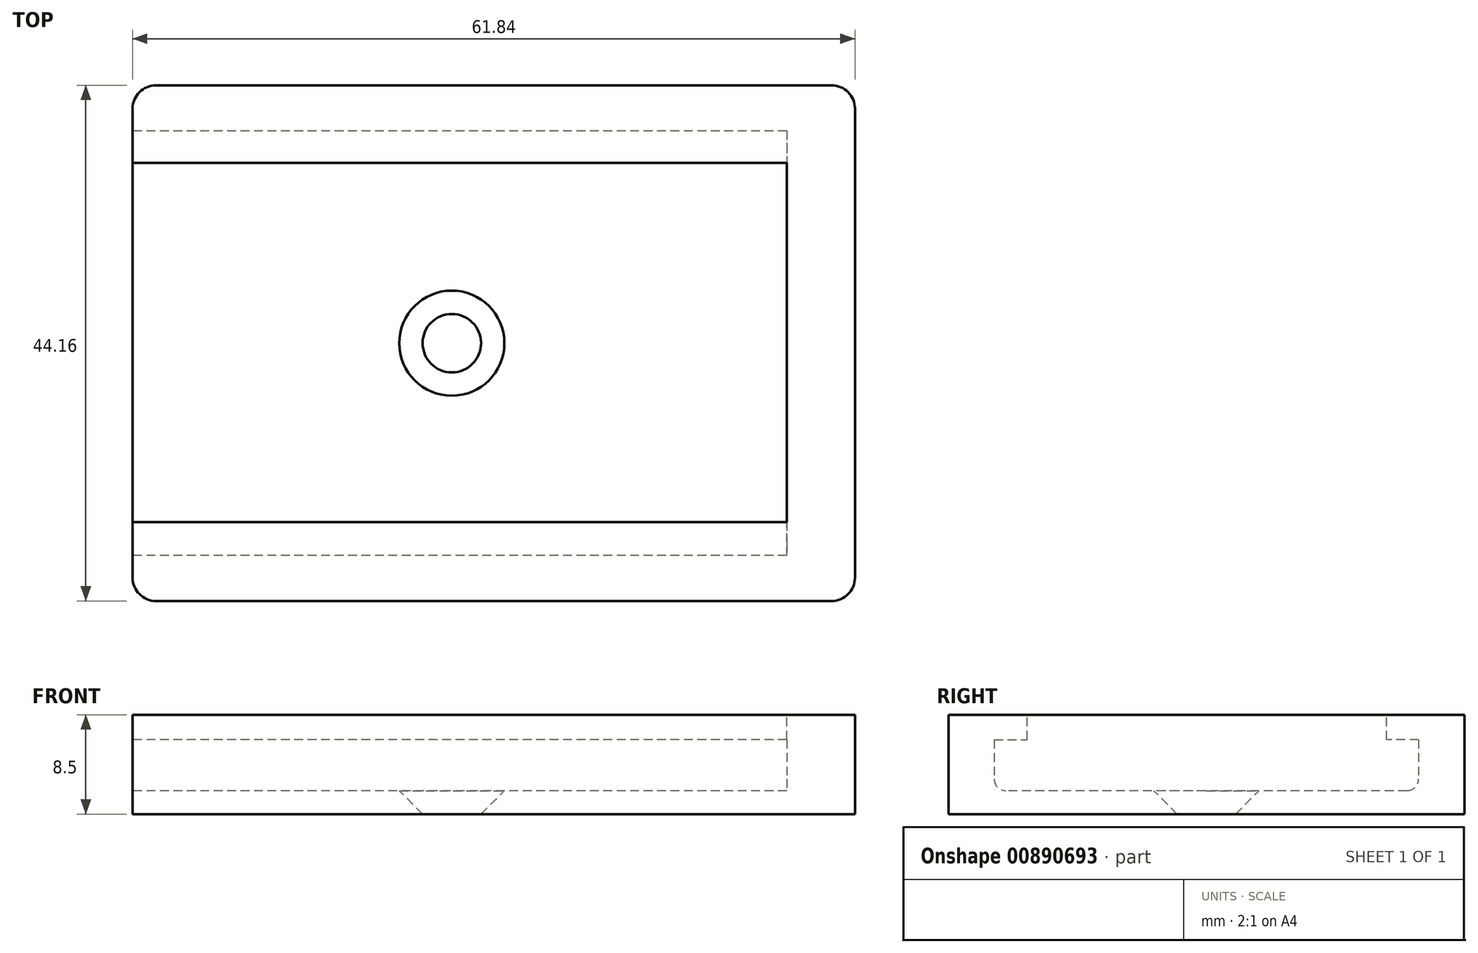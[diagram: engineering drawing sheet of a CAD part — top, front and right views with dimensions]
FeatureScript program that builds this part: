
annotation { "Feature Type Name" : "Feature", "Feature Type Description" : "" }
export const myFeature = defineFeature(function(context is Context, id is Id, definition is map)
    precondition{}
    {
        {
            var Q0;
            Q0=qCreatedBy(makeId("Top.planeOp"),FACE);
            var sketch = newSketch(context, id + "F0", { "sketchPlane" : qUnion([Q0])});
            skLineSegment(sketch, "E0.bottom", {"start": v(-27.33, 22.08) * mm, "end": v(34.5, 22.08) * mm});
            skLineSegment(sketch, "E0.top", {"start": v(-27.33, -22.08) * mm, "end": v(34.5, -22.08) * mm});
            skLineSegment(sketch, "E0.left", {"start": v(-27.33, 22.08) * mm, "end": v(-27.33, -22.08) * mm});
            skLineSegment(sketch, "E0.right", {"start": v(34.5, 22.08) * mm, "end": v(34.5, -22.08) * mm});
            skSolve(sketch);
        }
        {
            var Q0;
            Q0=makeQuery(id+"F0.imprint","IMPRINT",FACE,{"disambiguationData":[TD([[makeQuery(id+"F0.imprint","IMPRINT",EDGE,{"derivedFrom":sQuery(id+"F0.wireOp",EDGE,"E0.bottom")}),-1.0]])]});
            extrude(context, id + "F1", {"entities" : qUnion([Q0]), "depth" : 8.5 * mm, "offsetDistance" : 25 * mm});
        }
        {
            var Q0;
            Q0=makeQuery(id+"F1.opExtrude","SWEPT_EDGE",EDGE,{"disambiguationData":[OSD([sQuery(id+"F0.wireOp",EDGE,"E0.top"),sQuery(id+"F0.wireOp",EDGE,"E0.left")])]});
            var Q1;
            Q1=makeQuery(id+"F1.opExtrude","SWEPT_EDGE",EDGE,{"disambiguationData":[OSD([sQuery(id+"F0.wireOp",EDGE,"E0.top"),sQuery(id+"F0.wireOp",EDGE,"E0.right")])]});
            var Q2;
            Q2=makeQuery(id+"F1.opExtrude","SWEPT_EDGE",EDGE,{"disambiguationData":[OSD([sQuery(id+"F0.wireOp",EDGE,"E0.bottom"),sQuery(id+"F0.wireOp",EDGE,"E0.left")])]});
            var Q3;
            Q3=makeQuery(id+"F1.opExtrude","SWEPT_EDGE",EDGE,{"disambiguationData":[OSD([sQuery(id+"F0.wireOp",EDGE,"E0.bottom"),sQuery(id+"F0.wireOp",EDGE,"E0.right")])]});
            fillet(context, id + "F2", {"entities" : qUnion([Q0, Q1, Q2, Q3]), "tangentPropagation" : true, "radius" : 2 * mm, "defaultsChanged" : false, "vertexSettings" : [], "allowEdgeOverflow" : false});
        }
        {
            var Q0;
            Q0=makeQuery(id+"F1.opExtrude","SWEPT_FACE",FACE,{"disambiguationData":[OSD([sQuery(id+"F0.wireOp",EDGE,"E0.left")])]});
            var sketch = newSketch(context, id + "F3", { "sketchPlane" : qUnion([Q0])});
            skLineSegment(sketch, "E1.top", {"start": v(-17.17, 2) * mm, "end": v(17.17, 2) * mm});
            skLineSegment(sketch, "E1.left", {"start": v(-18.17, 6.37) * mm, "end": v(-18.17, 3) * mm});
            skLineSegment(sketch, "E1.right", {"start": v(18.17, 6.37) * mm, "end": v(18.17, 3) * mm});
            skPoint(sketch, "E2.visualSharp", {"position": v(-18.17, 2) * mm});
            skArc(sketch, "E2.filletArc", {"start": v(-18.17, 3) * mm, "mid": v(-17.87, 2.3) * mm, "end": v(-17.17, 2) * mm});
            skPoint(sketch, "E3.visualSharp", {"position": v(18.17, 2) * mm});
            skArc(sketch, "E3.filletArc", {"start": v(17.17, 2) * mm, "mid": v(17.87, 2.3) * mm, "end": v(18.17, 3) * mm});
            skLineSegment(sketch, "E4", {"start": v(-18.17, 6.37) * mm, "end": v(18.17, 6.37) * mm, "construction": true});
            skLineSegment(sketch, "E5", {"start": v(-18.17, 6.37) * mm, "end": v(-15.43, 6.37) * mm});
            skLineSegment(sketch, "E6", {"start": v(-15.43, 6.37) * mm, "end": v(-15.43, 8.5) * mm});
            skLineSegment(sketch, "E7", {"start": v(18.17, 6.37) * mm, "end": v(15.33, 6.37) * mm});
            skLineSegment(sketch, "E8", {"start": v(15.33, 6.37) * mm, "end": v(15.33, 8.5) * mm});
            skSolve(sketch);
        }
        {
            var Q0;
            Q0=makeQuery(id+"F3.imprint","IMPRINT",FACE,{"disambiguationData":[TD([[makeQuery(id+"F3.imprint","IMPRINT",EDGE,{"derivedFrom":sQuery(id+"F3.wireOp",EDGE,"E1.top")}),1.0]])]});
            extrude(context, id + "F4", {"entities" : qUnion([Q0]), "operationType" : NewBodyOperationType.REMOVE, "oppositeDirection" : true, "depth" : 56 * mm, "offsetDistance" : 25 * mm});
        }
        {
            var Q0;
            Q0=qCreatedBy(makeId("Top.planeOp"),FACE);
            var sketch = newSketch(context, id + "F5", { "sketchPlane" : qUnion([Q0])});
            skCircle(sketch, "E9", {"center": v(0, 0) * mm, "radius": 2.5 * mm});
            skSolve(sketch);
        }
        {
            var Q0;
            Q0 = qSketchRegion(id + "F5", true);
            extrude(context, id + "F6", {"entities" : qUnion([Q0]), "operationType" : NewBodyOperationType.REMOVE, "depth" : 25 * mm, "offsetDistance" : 25 * mm, "hasDraft" : true, "draftAngle" : 45 * degree});
        }
    });
